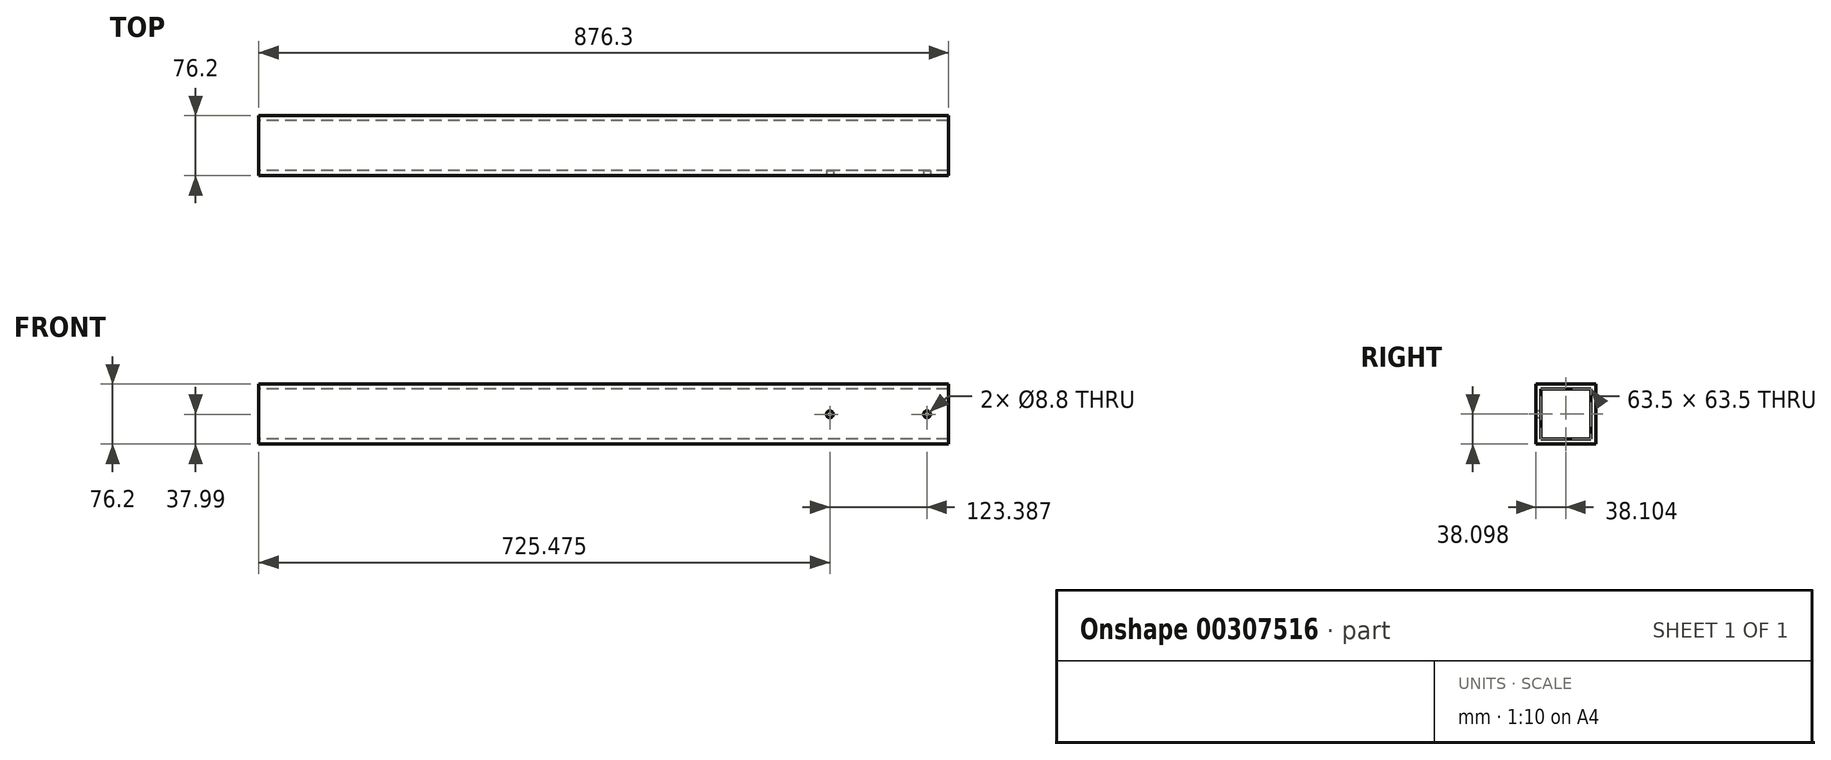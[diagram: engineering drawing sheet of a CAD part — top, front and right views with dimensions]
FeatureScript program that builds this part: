
annotation { "Feature Type Name" : "Feature", "Feature Type Description" : "" }
export const myFeature = defineFeature(function(context is Context, id is Id, definition is map)
    precondition{}
    {
        {
            var Q0;
            Q0=qCreatedBy(makeId("Right.planeOp"),FACE);
            var sketch = newSketch(context, id + "F0", { "sketchPlane" : qUnion([Q0])});
            skLineSegment(sketch, "E0.bottom", {"start": v(39.57, -38) * mm, "end": v(-36.63, -38) * mm});
            skLineSegment(sketch, "E0.top", {"start": v(39.57, 38.2) * mm, "end": v(-36.63, 38.2) * mm});
            skLineSegment(sketch, "E0.left", {"start": v(39.57, -38) * mm, "end": v(39.57, 38.2) * mm});
            skLineSegment(sketch, "E0.right", {"start": v(-36.63, -38) * mm, "end": v(-36.63, 38.2) * mm});
            skPoint(sketch, "E0.middle", {"position": v(1.47, 0.1) * mm});
            skPoint(sketch, "E1.visualSharp", {"position": v(-36.63, 38.2) * mm});
            skPoint(sketch, "E2.visualSharp", {"position": v(39.57, 38.2) * mm});
            skPoint(sketch, "E3.visualSharp", {"position": v(39.57, -38) * mm});
            skPoint(sketch, "E4.visualSharp", {"position": v(-36.63, -38) * mm});
            skLineSegment(sketch, "E5.bottom", {"start": v(33.22, -31.64) * mm, "end": v(-30.28, -31.64) * mm});
            skLineSegment(sketch, "E5.top", {"start": v(33.22, 31.86) * mm, "end": v(-30.28, 31.86) * mm});
            skLineSegment(sketch, "E5.left", {"start": v(33.22, -31.64) * mm, "end": v(33.22, 31.86) * mm});
            skLineSegment(sketch, "E5.right", {"start": v(-30.28, -31.64) * mm, "end": v(-30.28, 31.86) * mm});
            skPoint(sketch, "E6.visualSharp", {"position": v(-30.28, 31.86) * mm});
            skPoint(sketch, "E7.visualSharp", {"position": v(33.22, 31.86) * mm});
            skPoint(sketch, "E8.visualSharp", {"position": v(33.22, -31.64) * mm});
            skPoint(sketch, "E9.visualSharp", {"position": v(-30.28, -31.64) * mm});
            skSolve(sketch);
        }
        {
            var Q0;
            Q0 = qSketchRegion(id + "F0", true);
            extrude(context, id + "F1", {"entities" : qUnion([Q0]), "depth" : 876.3 * mm});
        }
        {
            var Q0;
            Q0=makeQuery(id+"F1.opExtrude","SWEPT_FACE",FACE,{"disambiguationData":[OSD([sQuery(id+"F0.wireOp",EDGE,"E0.right")])]});
            cPlane(context, id + "F2", {"entities" : qUnion([Q0]), "cplaneType" : CPlaneType.OFFSET, "offset" : 0 * mm, "width" : 150 * mm, "height" : 150 * mm});
        }
        {
            var Q0;
            Q0=qCreatedBy(id+"F2.planeOp",FACE);
            var sketch = newSketch(context, id + "F3", { "sketchPlane" : qUnion([Q0])});
            skLineSegment(sketch, "E10.bottom", {"start": v(875.86, 32.28) * mm, "end": v(698.06, 32.28) * mm});
            skLineSegment(sketch, "E10.top", {"start": v(875.86, -32.74) * mm, "end": v(698.06, -32.74) * mm});
            skLineSegment(sketch, "E10.left", {"start": v(875.86, 32.28) * mm, "end": v(875.86, -32.74) * mm});
            skLineSegment(sketch, "E10.right", {"start": v(698.06, 32.28) * mm, "end": v(698.06, -32.74) * mm});
            skPoint(sketch, "E11", {"position": v(848.86, 0) * mm});
            skPoint(sketch, "E12", {"position": v(725.47, 0) * mm});
            skSolve(sketch);
        }
        {
            var Q0;
            Q0=sQuery(id+"F3.wireOp",VERTEX,"E11");
            var Q1;
            Q1=sQuery(id+"F3.wireOp",VERTEX,"E12");
            var Q2;
            Q2=makeQuery(id+"F1.opExtrude","SWEPT_BODY",BODY,{"disambiguationData":[OSD([sQuery(id+"F0.wireOp",EDGE,"E0.bottom"),sQuery(id+"F0.wireOp",EDGE,"E0.top"),sQuery(id+"F0.wireOp",EDGE,"E0.left"),sQuery(id+"F0.wireOp",EDGE,"E0.right"),sQuery(id+"F0.wireOp",EDGE,"E1.filletArc"),sQuery(id+"F0.wireOp",EDGE,"E2.filletArc"),sQuery(id+"F0.wireOp",EDGE,"E3.filletArc"),sQuery(id+"F0.wireOp",EDGE,"E4.filletArc"),sQuery(id+"F0.wireOp",EDGE,"E5.bottom"),sQuery(id+"F0.wireOp",EDGE,"E5.top"),sQuery(id+"F0.wireOp",EDGE,"E5.left"),sQuery(id+"F0.wireOp",EDGE,"E5.right"),sQuery(id+"F0.wireOp",EDGE,"E6.filletArc"),sQuery(id+"F0.wireOp",EDGE,"E7.filletArc"),sQuery(id+"F0.wireOp",EDGE,"E8.filletArc"),sQuery(id+"F0.wireOp",EDGE,"E9.filletArc")])]});
            hole(context, id + "F4", {"style" : HoleStyle.SIMPLE, "endStyle" : HoleEndStyle.BLIND, "standardTappedOrClearance" : lookupTablePath({ "standard" : "ISO", "fit" : "Normal", "size" : "M8", "type" : "Clearance" }), "standardBlindInLast" : lookupTablePath({ "fit" : "Standard", "standard" : "ISO", "size" : "M8", "type" : "Clearance" }), "holeDiameter" : 8.8 * mm, "holeDepth" : 29.15 * mm, "tappedDepth" : 25.4 * mm, "tapClearance" : 3, "locations" : qUnion([Q0, Q1]), "scope" : qUnion([Q2])});
        }
    });
